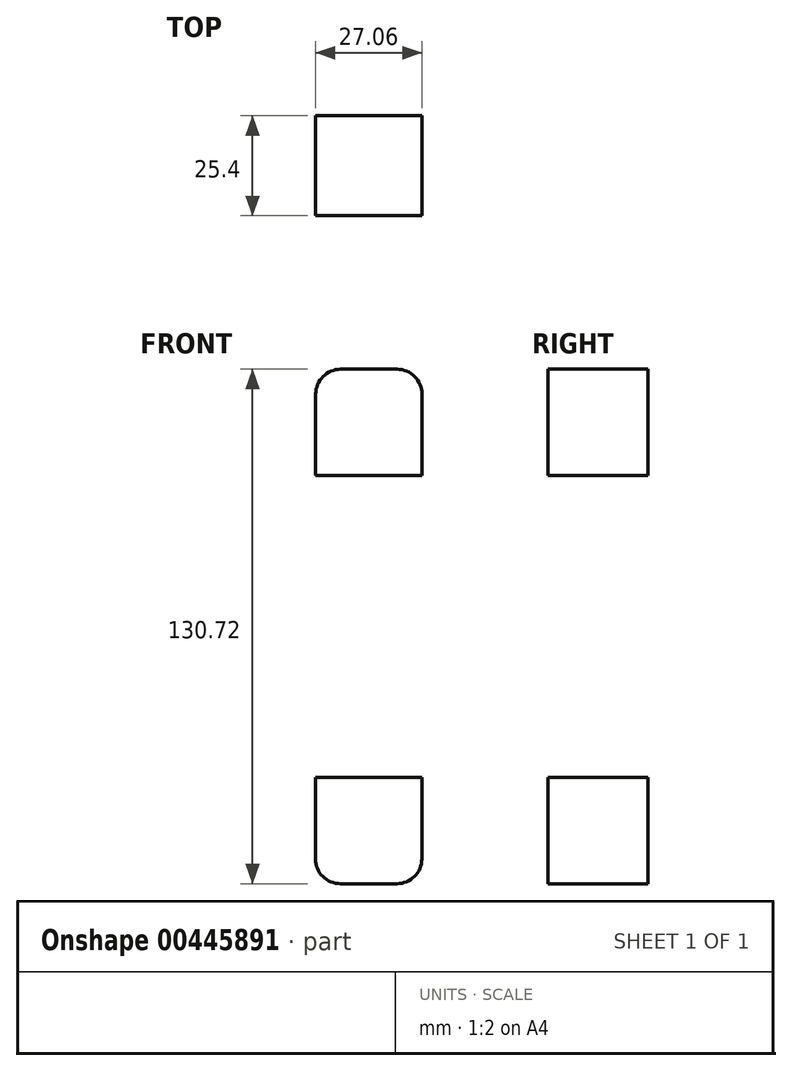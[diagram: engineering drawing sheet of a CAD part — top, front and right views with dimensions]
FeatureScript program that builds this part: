
annotation { "Feature Type Name" : "Feature", "Feature Type Description" : "" }
export const myFeature = defineFeature(function(context is Context, id is Id, definition is map)
    precondition{}
    {
        {
            var Q0;
            Q0=qCreatedBy(makeId("Front.planeOp"),FACE);
            var sketch = newSketch(context, id + "F0", { "sketchPlane" : qUnion([Q0])});
            skLineSegment(sketch, "E0.bottom", {"start": v(-39.41, 59.87) * mm, "end": v(-25.11, 59.87) * mm});
            skLineSegment(sketch, "E0.top", {"start": v(-45.76, 32.87) * mm, "end": v(-18.76, 32.87) * mm});
            skLineSegment(sketch, "E0.left", {"start": v(-45.76, 53.52) * mm, "end": v(-45.76, 32.87) * mm});
            skLineSegment(sketch, "E0.right", {"start": v(-18.76, 53.52) * mm, "end": v(-18.76, 32.87) * mm});
            skPoint(sketch, "E1.visualSharp", {"position": v(-45.76, 59.87) * mm});
            skArc(sketch, "E1.filletArc", {"start": v(-39.41, 59.87) * mm, "mid": v(-43.9, 58) * mm, "end": v(-45.76, 53.52) * mm});
            skPoint(sketch, "E2.visualSharp", {"position": v(-18.76, 59.87) * mm});
            skArc(sketch, "E2.filletArc", {"start": v(-18.76, 53.52) * mm, "mid": v(-20.62, 58) * mm, "end": v(-25.11, 59.87) * mm});
            skLineSegment(sketch, "E3.bottom", {"start": v(-25.17, -70.85) * mm, "end": v(-39.47, -70.85) * mm});
            skLineSegment(sketch, "E3.top", {"start": v(-18.82, -43.85) * mm, "end": v(-45.82, -43.85) * mm});
            skLineSegment(sketch, "E3.left", {"start": v(-18.82, -64.5) * mm, "end": v(-18.82, -43.85) * mm});
            skLineSegment(sketch, "E3.right", {"start": v(-45.82, -64.5) * mm, "end": v(-45.82, -43.85) * mm});
            skPoint(sketch, "E4.visualSharp", {"position": v(-18.82, -70.85) * mm});
            skArc(sketch, "E4.filletArc", {"start": v(-25.17, -70.85) * mm, "mid": v(-20.68, -69) * mm, "end": v(-18.82, -64.5) * mm});
            skPoint(sketch, "E5.visualSharp", {"position": v(-45.82, -70.85) * mm});
            skArc(sketch, "E5.filletArc", {"start": v(-45.82, -64.5) * mm, "mid": v(-43.96, -69) * mm, "end": v(-39.47, -70.85) * mm});
            skSolve(sketch);
        }
        {
            var Q0;
            Q0 = qSketchRegion(id + "F0", true);
            extrude(context, id + "F1", {"entities" : qUnion([Q0]), "depth" : 25.4 * mm});
        }
    });
